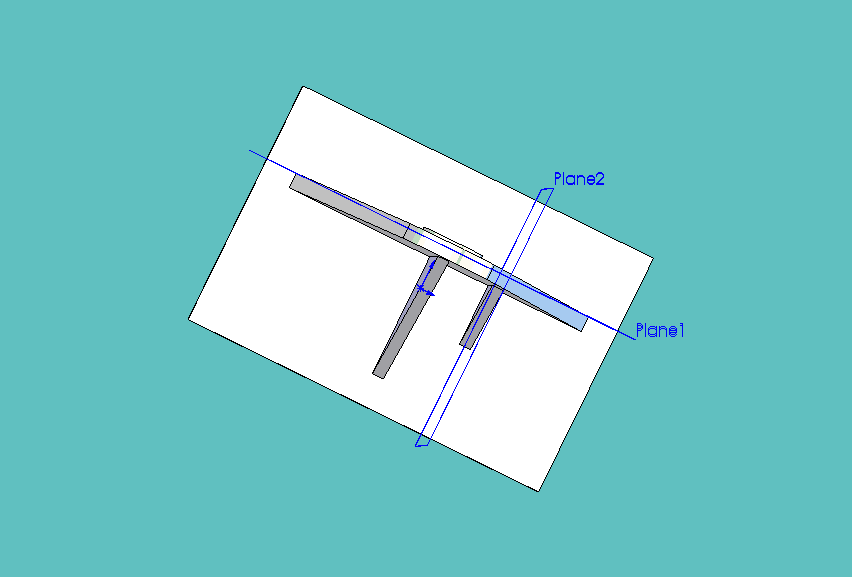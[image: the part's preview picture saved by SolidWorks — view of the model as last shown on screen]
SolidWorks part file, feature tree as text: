
SOLIDWORKS PART (.sldprt)
format: sldprt  version: not decoded by parser v0  size: 234,496 bytes
history: native  units: mm
features: plane x5, sketch x5, extrude x4, material x1 (+10 scaffold rows collapsed)
feature tree (25):
  scaffold x10  (default folders/planes/origin — collapsed)
  material  "Material <not specified>"
  plane  "Frontal"
  plane  "Horizontal"
  plane  "Profile"
  sketch  "Sketch1"  dims[D1=152.4mm D2=101.6mm]
  extrude  "Extrude1"  Depth=6.35mm
  plane  "Plane1"  Offset=31.75mm
  sketch  "Sketch3"  dims[D3=19.05mm D1=127.0mm D2=177.8mm]
  extrude  "Extrude2"  Depth=6.35mm
  sketch  "Sketch4"  dims[D1=25.4mm]
  extrude  "Extrude3"  Depth=1.27mm
  sketch  "Sketch5"  dims[D1=139.7mm D2=50.8mm]
  extrude  "Extrude4"  Depth=4.7625mm
  plane  "Plane2"  Offset=25.4mm
  sketch  "Sketch8"  dims[c1.D1=25.4mm c2.D1=4.7625mm]
decode coverage: 9 of 9 modeling features carry decoded parameters
note: suppression state not decoded; provenance and decode notes live in map.json
